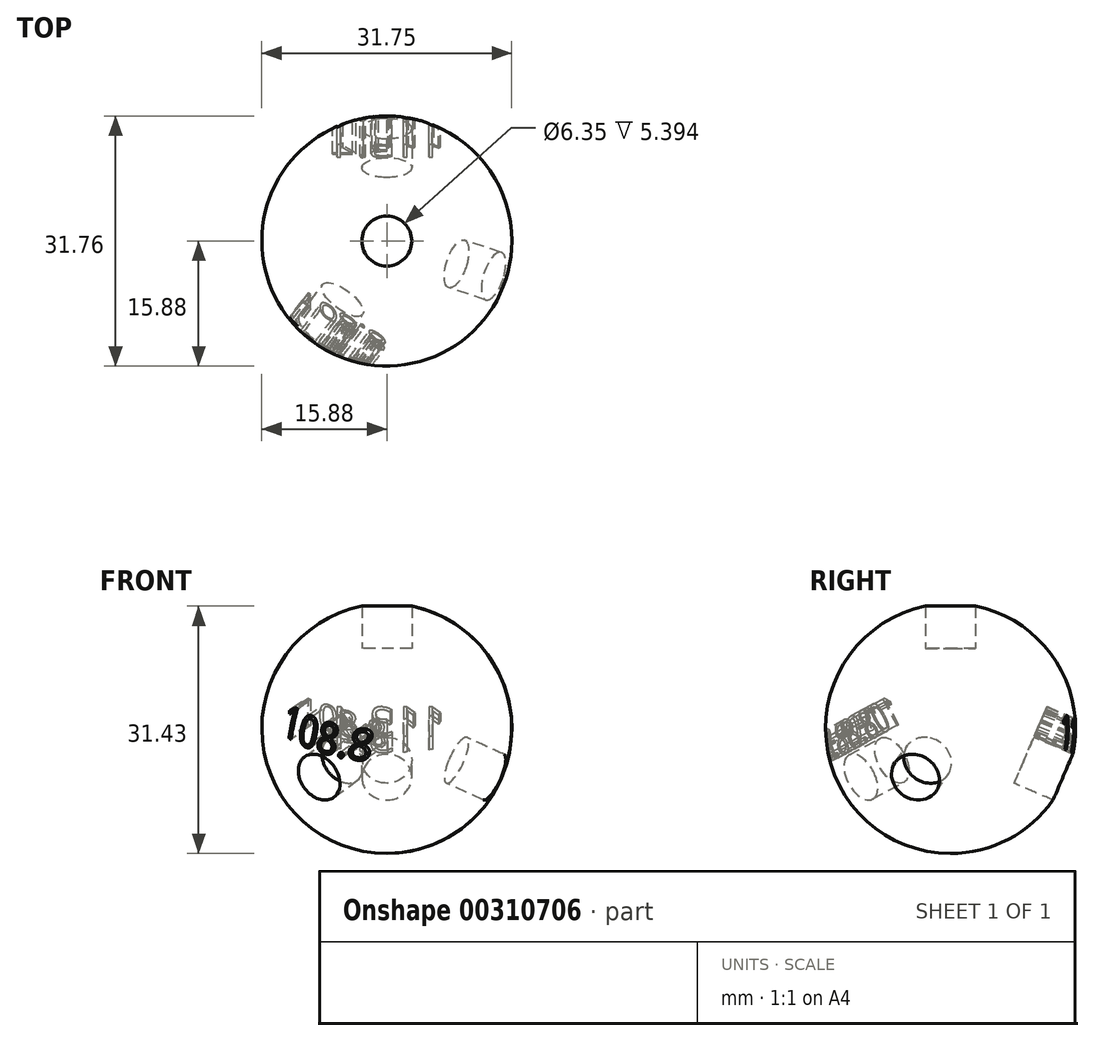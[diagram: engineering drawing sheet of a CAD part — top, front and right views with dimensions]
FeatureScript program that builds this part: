
annotation { "Feature Type Name" : "Feature", "Feature Type Description" : "" }
export const myFeature = defineFeature(function(context is Context, id is Id, definition is map)
    precondition{}
    {
        {
            var Q0;
            Q0=qCreatedBy(makeId("Front.planeOp"),FACE);
            var sketch = newSketch(context, id + "F0", { "sketchPlane" : qUnion([Q0])});
            skArc(sketch, "E0", {"start": v(0, 15.88) * mm, "mid": v(-15.88, 0) * mm, "end": v(0, -15.88) * mm});
            skLineSegment(sketch, "E1", {"start": v(0, 15.88) * mm, "end": v(0, -15.88) * mm});
            skSolve(sketch);
        }
        {
            var Q0;
            Q0=qCreatedBy(makeId("Top.planeOp"),FACE);
            var sketch = newSketch(context, id + "F1", { "sketchPlane" : qUnion([Q0])});
            skCircle(sketch, "E2", {"center": v(0, 0) * mm, "radius": 15.88 * mm});
            skSolve(sketch);
        }
        {
            var Q0;
            Q0=makeQuery(id+"F0.imprint","IMPRINT",FACE,{"disambiguationData":[TD([[makeQuery(id+"F0.imprint","IMPRINT",EDGE,{"derivedFrom":sQuery(id+"F0.wireOp",EDGE,"E0")}),1.0]])]});
            var Q1;
            Q1=sQuery(id+"F1.wireOp",EDGE,"E2");
            revolve(context, id + "F2", {"entities" : qUnion([Q0]), "axis" : qUnion([Q1]), "revolveType" : RevolveType.FULL});
        }
        {
            var Q0;
            Q0=qCreatedBy(makeId("Top.planeOp"),FACE);
            cPlane(context, id + "F3", {"entities" : qUnion([Q0]), "cplaneType" : CPlaneType.OFFSET, "offset" : 10.16 * mm, "width" : 152.4 * mm, "height" : 152.4 * mm});
        }
        {
            var Q0;
            Q0=qCreatedBy(id+"F3.planeOp",FACE);
            var sketch = newSketch(context, id + "F4", { "sketchPlane" : qUnion([Q0])});
            skCircle(sketch, "E3", {"center": v(0, 0) * mm, "radius": 3.18 * mm});
            skSolve(sketch);
        }
        {
            var Q0;
            Q0=qSketchRegion(id+"F4",true);
            extrude(context, id + "F5", {"entities" : qUnion([Q0]), "depth" : 50.8 * mm});
        }
        {
            var Q0;
            Q0=qCreatedBy(makeId("Front.planeOp"),FACE);
            var sketch = newSketch(context, id + "F6", { "sketchPlane" : qUnion([Q0])});
            skLineSegment(sketch, "E4", {"start": v(0, 0) * mm, "end": v(0, -58.07) * mm, "construction": true});
            skLineSegment(sketch, "E5", {"start": v(0, 0) * mm, "end": v(-72.63, 0) * mm, "construction": true});
            skSolve(sketch);
        }
        {
            var Q0;
            Q0=makeQuery(id+"F5.opExtrude","SWEPT_BODY",BODY,{"disambiguationData":[OSD([sQuery(id+"F4.wireOp",EDGE,"E3")])]});
            var Q1;
            Q1=sQuery(id+"F6.wireOp",EDGE,"E5");
            transform(context, id + "F7", {"entities" : qUnion([Q0]), "transformType" : TransformType.ROTATION, "transformAxis" : qUnion([Q1]), "angle" : 113.4 * degree, "makeCopy" : true});
        }
        {
            var Q0;
            Q0=makeQuery(id+"F7.opPattern","COPY",BODY,{"derivedFrom":makeQuery(id+"F5.opExtrude","SWEPT_BODY",BODY,{"disambiguationData":[OSD([sQuery(id+"F4.wireOp",EDGE,"E3")])]}),"instanceName":"1"});
            var Q1;
            Q1=sQuery(id+"F6.wireOp",EDGE,"E4");
            transform(context, id + "F8", {"entities" : qUnion([Q0]), "transformType" : TransformType.ROTATION, "transformAxis" : qUnion([Q1]), "angle" : 108.2 * degree, "makeCopy" : true});
        }
        {
            var Q0;
            Q0=makeQuery(id+"F8.opPattern","COPY",BODY,{"derivedFrom":makeQuery(id+"F7.opPattern","COPY",BODY,{"derivedFrom":makeQuery(id+"F5.opExtrude","SWEPT_BODY",BODY,{"disambiguationData":[OSD([sQuery(id+"F4.wireOp",EDGE,"E3")])]}),"instanceName":"1"}),"instanceName":"1"});
            var Q1;
            Q1=sQuery(id+"F6.wireOp",EDGE,"E4");
            transform(context, id + "F9", {"entities" : qUnion([Q0]), "transformType" : TransformType.ROTATION, "transformAxis" : qUnion([Q1]), "angle" : 108.8 * degree, "makeCopy" : true});
        }
        {
            var Q0;
            Q0=makeQuery(id+"F7.opPattern","COPY",FACE,{"derivedFrom":makeQuery(id+"F5.opExtrude","CAP_FACE",FACE,{"disambiguationData":[OSD([sQuery(id+"F4.wireOp",EDGE,"E3")])],"isStart":false}),"instanceName":"1"});
            cPlane(context, id + "F10", {"entities" : qUnion([Q0]), "cplaneType" : CPlaneType.OFFSET, "offset" : 25.4 * mm, "oppositeDirection" : true, "width" : 152.4 * mm, "height" : 152.4 * mm});
        }
        {
            var Q0;
            Q0=qCreatedBy(id+"F10.planeOp",FACE);
            var sketch = newSketch(context, id + "F11", { "sketchPlane" : qUnion([Q0])});
            skText(sketch, "E6", { "text": "113.4", "fontName": "OpenSans-Regular.ttf"});
            const initialGuessF11  = {"E6": [-0.00732, 0.00336, 1, 0, 0.00404]};
            skSetInitialGuess(sketch, initialGuessF11);
            skSolve(sketch);
        }
        {
            var Q0;
            Q0=qSketchRegion(id+"F11",true);
            extrude(context, id + "F12", {"entities" : qUnion([Q0]), "operationType" : NewBodyOperationType.REMOVE, "oppositeDirection" : true, "depth" : 25.4 * mm});
        }
        {
            var Q0;
            Q0=makeQuery(id+"F9.opPattern","COPY",FACE,{"derivedFrom":makeQuery(id+"F8.opPattern","COPY",FACE,{"derivedFrom":makeQuery(id+"F7.opPattern","COPY",FACE,{"derivedFrom":makeQuery(id+"F5.opExtrude","CAP_FACE",FACE,{"disambiguationData":[OSD([sQuery(id+"F4.wireOp",EDGE,"E3")])],"isStart":false}),"instanceName":"1"}),"instanceName":"1"}),"instanceName":"1"});
            cPlane(context, id + "F13", {"entities" : qUnion([Q0]), "cplaneType" : CPlaneType.OFFSET, "offset" : 25.4 * mm, "oppositeDirection" : true, "width" : 152.4 * mm, "height" : 152.4 * mm});
        }
        {
            var Q0;
            Q0=qCreatedBy(id+"F13.planeOp",FACE);
            var sketch = newSketch(context, id + "F14", { "sketchPlane" : qUnion([Q0])});
            skText(sketch, "E7", { "text": "108.8\n", "fontName": "OpenSans-Regular.ttf"});
            const initialGuessF14  = {"E7": [-0.0067, 0.0036, 1, 0, 0.00379]};
            skSetInitialGuess(sketch, initialGuessF14);
            skSolve(sketch);
        }
        {
            var Q0;
            Q0=qSketchRegion(id+"F14",true);
            extrude(context, id + "F15", {"entities" : qUnion([Q0]), "operationType" : NewBodyOperationType.REMOVE, "oppositeDirection" : true, "depth" : 25.4 * mm});
        }
        {
            var Q0;
            Q0=makeQuery(id+"F5.opExtrude","SWEPT_BODY",BODY,{"disambiguationData":[OSD([sQuery(id+"F4.wireOp",EDGE,"E3")])]});
            var Q1;
            Q1=makeQuery(id+"F7.opPattern","COPY",BODY,{"derivedFrom":makeQuery(id+"F5.opExtrude","SWEPT_BODY",BODY,{"disambiguationData":[OSD([sQuery(id+"F4.wireOp",EDGE,"E3")])]}),"instanceName":"1"});
            var Q2;
            Q2=makeQuery(id+"F9.opPattern","COPY",BODY,{"derivedFrom":makeQuery(id+"F8.opPattern","COPY",BODY,{"derivedFrom":makeQuery(id+"F7.opPattern","COPY",BODY,{"derivedFrom":makeQuery(id+"F5.opExtrude","SWEPT_BODY",BODY,{"disambiguationData":[OSD([sQuery(id+"F4.wireOp",EDGE,"E3")])]}),"instanceName":"1"}),"instanceName":"1"}),"instanceName":"1"});
            var Q3;
            Q3=makeQuery(id+"F8.opPattern","COPY",BODY,{"derivedFrom":makeQuery(id+"F7.opPattern","COPY",BODY,{"derivedFrom":makeQuery(id+"F5.opExtrude","SWEPT_BODY",BODY,{"disambiguationData":[OSD([sQuery(id+"F4.wireOp",EDGE,"E3")])]}),"instanceName":"1"}),"instanceName":"1"});
            var Q4;
            Q4=makeQuery(id+"F2.opRevolve","SWEPT_BODY",BODY,{"disambiguationData":[OSD([sQuery(id+"F0.wireOp",EDGE,"E0"),sQuery(id+"F0.wireOp",EDGE,"E1")])]});
            booleanBodies(context, id + "F16", {"operationType" : BooleanOperationType.SUBTRACTION, "tools" : qUnion([Q0, Q1, Q2, Q3]), "targets" : qUnion([Q4])});
        }
    });
